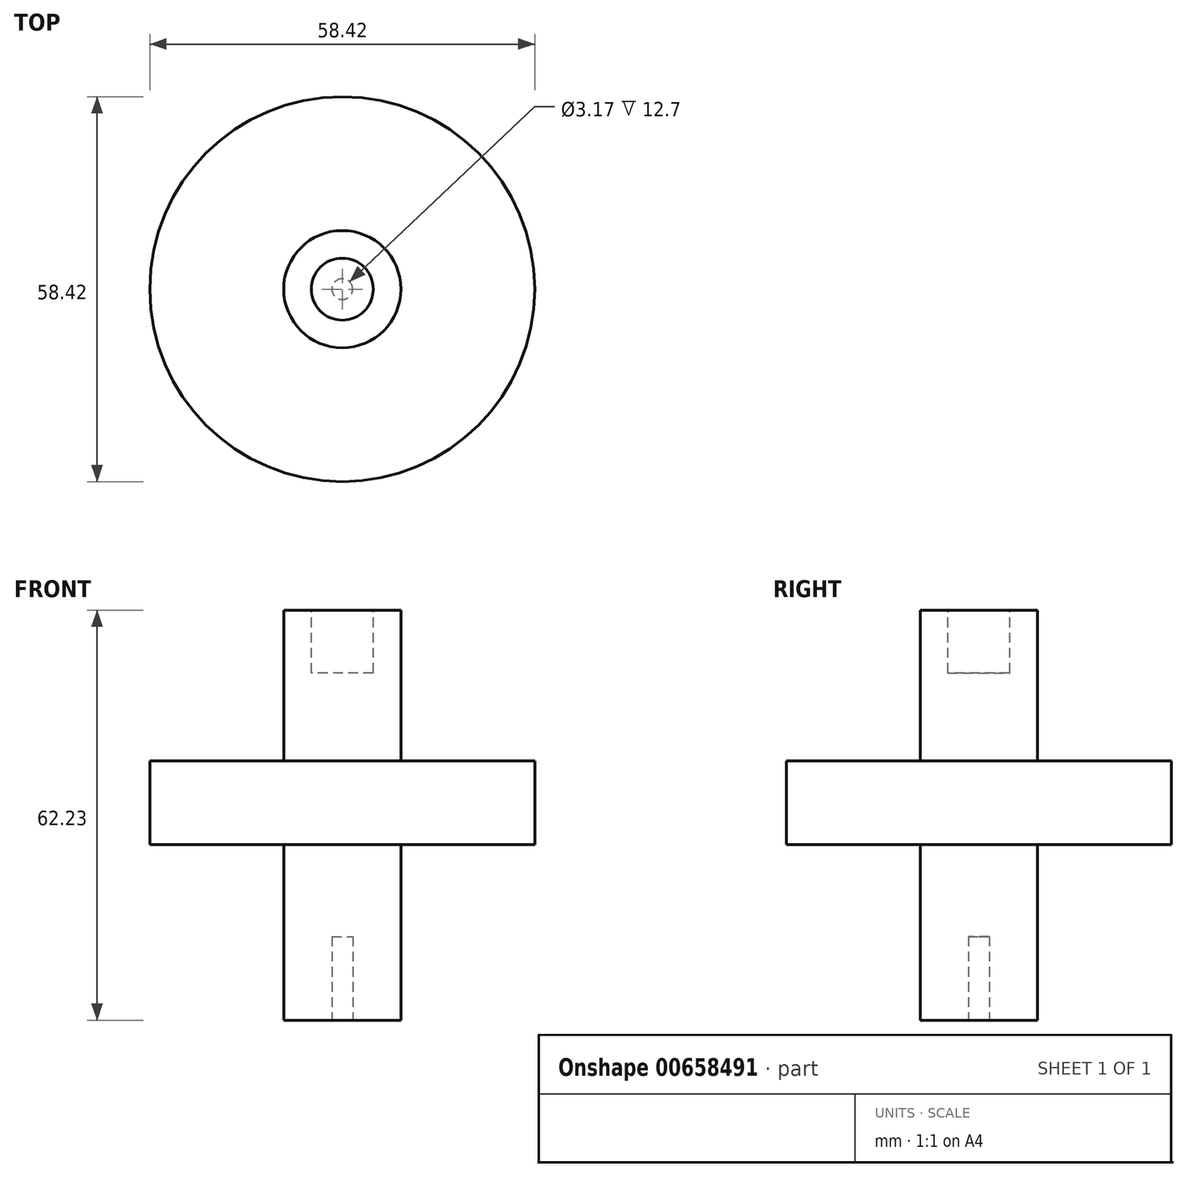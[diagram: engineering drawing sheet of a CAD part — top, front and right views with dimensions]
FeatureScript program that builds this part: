
annotation { "Feature Type Name" : "Feature", "Feature Type Description" : "" }
export const myFeature = defineFeature(function(context is Context, id is Id, definition is map)
    precondition{}
    {
        {
            var Q0;
            Q0=qCreatedBy(makeId("Front.planeOp"),FACE);
            var sketch = newSketch(context, id + "F0", { "sketchPlane" : qUnion([Q0])});
            skLineSegment(sketch, "E0", {"start": v(0, 0) * mm, "end": v(8.9, 0) * mm});
            skLineSegment(sketch, "E1", {"start": v(8.9, 0) * mm, "end": v(8.9, 39.37) * mm});
            skLineSegment(sketch, "E2", {"start": v(8.9, 39.37) * mm, "end": v(29.21, 39.37) * mm});
            skLineSegment(sketch, "E3", {"start": v(29.21, 26.67) * mm, "end": v(29.21, 39.37) * mm});
            skLineSegment(sketch, "E4", {"start": v(29.21, 26.67) * mm, "end": v(8.9, 26.67) * mm});
            skLineSegment(sketch, "E5", {"start": v(8.9, 26.67) * mm, "end": v(8.9, 62.23) * mm});
            skLineSegment(sketch, "E6", {"start": v(8.9, 62.23) * mm, "end": v(0, 62.23) * mm});
            skLineSegment(sketch, "E7", {"start": v(0, 62.23) * mm, "end": v(0, 0) * mm});
            skSolve(sketch);
        }
        {
            var Q0;
            Q0=qSketchRegion(id+"F0",true);
            var Q1;
            Q1=sQuery(id+"F0.wireOp",EDGE,"E7");
            revolve(context, id + "F1", {"entities" : qUnion([Q0]), "axis" : qUnion([Q1]), "revolveType" : RevolveType.FULL});
        }
        {
            var Q0;
            Q0=makeQuery(id+"F1.opRevolve","SWEPT_FACE",FACE,{"disambiguationData":[OSD([sQuery(id+"F0.wireOp",EDGE,"E6")])]});
            var sketch = newSketch(context, id + "F2", { "sketchPlane" : qUnion([Q0])});
            skCircle(sketch, "E8", {"center": v(0, 0) * mm, "radius": 4.7 * mm});
            skSolve(sketch);
        }
        {
            var Q0;
            Q0=qSketchRegion(id+"F2",true);
            extrude(context, id + "F3", {"entities" : qUnion([Q0]), "operationType" : NewBodyOperationType.REMOVE, "oppositeDirection" : true, "depth" : 9.52 * mm, "offsetDistance" : 25.4 * mm});
        }
        {
            var Q0;
            Q0=makeQuery(id+"F1.opRevolve","SWEPT_FACE",FACE,{"disambiguationData":[OSD([sQuery(id+"F0.wireOp",EDGE,"E0")])]});
            var sketch = newSketch(context, id + "F4", { "sketchPlane" : qUnion([Q0])});
            skCircle(sketch, "E9", {"center": v(0, 0) * mm, "radius": 1.59 * mm});
            skSolve(sketch);
        }
        {
            var Q0;
            Q0=qSketchRegion(id+"F4",true);
            extrude(context, id + "F5", {"entities" : qUnion([Q0]), "operationType" : NewBodyOperationType.REMOVE, "oppositeDirection" : true, "depth" : 12.7 * mm, "offsetDistance" : 25.4 * mm});
        }
    });
